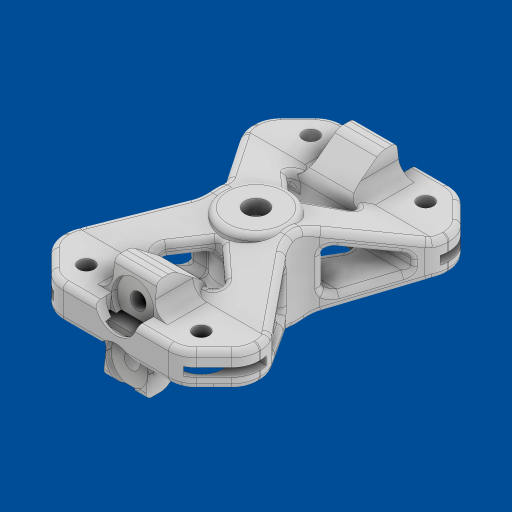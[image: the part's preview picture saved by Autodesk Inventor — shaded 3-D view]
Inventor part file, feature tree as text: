
AUTODESK INVENTOR PART (.ipt)
format: ipt  version: 2023 (Build 270158000, 158)  size: 1,712,640 bytes
history: native  units: mm
features: extrude x20, fillet x18, sketch x6, chamfer x4, mirror x3, plane x1, loft x1, other x1
ambient origin geometry x8: Origin, YZ Plane, XZ Plane, XY Plane, X Axis, Y Axis, Z Axis, Center Point
bodies: Body1 (feature_tree)
feature tree (54):
  sketch  "Sketch1"  dims[d13=261.822mm d14=7.45mm]
  plane  "Work Plane1"
  sketch  "Sketch2"  dims[d15=27.223mm d17=1.0mm]
  extrude  "Extrusion26"  Depth=7.45mm
  extrude  "Extrusion27"  Depth=1.0mm
  loft  "Loft4"
  extrude  "Extrusion30"  Depth=1.0mm
  extrude  "Extrusion32"  Depth=1.0mm
  extrude  "Extrusion33"  Depth=15.0mm
  chamfer  "Chamfer7"  Distance=65.0mm
  chamfer  "Chamfer8"  Distance=12.0mm
  fillet  "Fillet9"  Radius=1.0mm
  mirror  "Mirror1"
  extrude  "Extrusion45"  Depth=15.0mm
  extrude  "Extrusion48"  Depth=15.0mm TaperAngle=0.0deg
  extrude  "Extrusion49"  Depth=15.0mm
  sketch  "Sketch17"  dims[d23=2.0mm d25=1.0mm]
  extrude  "Extrusion51"  Depth=15.0mm
  fillet  "Fillet30"  Radius=30.0mm
  extrude  "Extrusion54"  Depth=5.0mm TaperAngle=0.0deg
  extrude  "Extrusion55"  Depth=15.0mm
  extrude  "Extrusion57"  TaperAngle=0.0deg  [1 undecoded]
  extrude  "Extrusion58"  TaperAngle=0.0deg  [1 undecoded]
  extrude  "Extrusion59"  Depth=15.0mm TaperAngle=0.0deg
  extrude  "Extrusion60"  Depth=15.0mm
  chamfer  "Chamfer15"  Distance=15.0mm
  chamfer  "Chamfer16"  Distance=15.0mm
  mirror  "Mirror3"
  extrude  "Extrusion61"  Depth=15.0mm TaperAngle=45.0deg
  extrude  "Extrusion62"  Depth=15.0mm TaperAngle=45.0deg
  extrude  "Extrusion63"  Depth=10.0mm
  fillet  "Fillet34"  Radius=15.0mm
  fillet  "Fillet35"  Radius=30.0mm
  fillet  "Fillet37"  Radius=14.0mm
  fillet  "Fillet38"  Radius=100.0mm
  extrude  "Extrusion64"  Depth=10.0mm
  mirror  "Mirror4"
  fillet  "Fillet39"  Radius=100.0mm
  fillet  "Fillet42"  Radius=15.0mm
  fillet  "Fillet43"  Radius=15.0mm
  fillet  "Fillet44"  Radius=15.0mm
  fillet  "Fillet45"  Radius=15.0mm
  fillet  "Fillet46"  Radius=7.5mm
  fillet  "Fillet47"  Radius=15.0mm
  fillet  "Fillet48"  Radius=5.5mm
  fillet  "Fillet49"  Radius=15.0mm
  fillet  "Fillet50"  Radius=2.5mm
  fillet  "Fillet51"  Radius=15.0mm
  fillet  "Fillet52"  Radius=15.0mm
  extrude  "Extrusion66"  Depth=15.0mm
  sketch  "Sketch12"  dims[d21=35.0mm d22=100.0mm]
  other  "Edges5"
  sketch  "Sketch18"  dims[d26=90.0deg d27=1.0mm]
  sketch  "Sketch19"  dims[d28=90.0deg d29=5.5mm d30=15.0mm d31=65.0mm d56=12.0mm d74=1.0mm d75=8.0mm d148=244.423mm d149=41.005864mm d150=244.423mm d151=5.5mm d152=5.5mm d153=5.5mm d154=15.0mm d155=15.0mm d156=18.0mm d157=5.5mm d158=160.0mm d159=7.0mm d160=0.0mm d161=8.0mm d162=24.0mm d163=30.0mm d164=0.0mm d165=5.0mm d166=0.0mm d167=19.96mm d170=0.0mm d171=90.0deg d172=0.0mm d173=90.0deg d178=2.0mm d179=0.0mm d180=2.0mm d183=15.0mm d184=0.0mm d185=15.0mm d186=0.0mm d206=12.0mm d207=12.0mm d208=45.0deg d209=12.0mm d210=12.0mm d211=45.0deg d212=10.0mm d256=15.0mm d257=30.0mm d258=0.0mm d271=14.0mm d272=100.0mm d273=10.0mm d274=100.0mm d276=15.0mm d277=0.0mm d287=15.0mm d288=0.0mm d289=15.0mm d290=15.0mm d291=7.5mm d292=15.0mm d293=5.5mm d296=15.0mm d297=2.5mm d298=15.0mm d299=15.0mm d300=7.5mm d301=15.0mm d302=5.5mm d303=15.0mm d304=0.0mm d310=2.0mm d311=2.0mm d312=0.0mm d313=5.0mm d316=5.0mm d317=5.0mm d318=16.0mm d319=100.0mm d320=0.0mm d324=35.0mm d325=0.0mm d326=40.0mm d327=0.0mm d328=20.0mm d329=0.0mm d330=12.0mm d331=0.0mm d333=5.0mm d334=12.0mm d335=9.168mm d336=45.0deg d337=15.0mm d338=10.835mm d339=45.0deg d341=5.0mm d342=30.0mm d343=0.0mm d344=30.0mm d345=0.0mm d346=30.0mm d347=0.0mm d348=10.0mm d349=10.0mm d351=2.0mm d352=2.0mm d353=2.0mm d354=0.0mm d355=2.0mm d358=2.0mm d359=2.0mm d360=2.0mm d361=2.0mm d362=2.0mm d363=2.0mm d364=2.0mm d365=2.0mm d366=2.0mm d367=5.0mm d368=5.0mm d369=1.0mm d370=0.0mm d373=10.0mm d374=0.0mm d375=15.0mm d376=0.0mm d76=0.5mm d77=0.872665mm d144=0.5mm d145=0.872665mm d146=0.5mm d147=0.872665mm d241=0.0mm d242=0.0mm d243=0.0mm d244=0.0mm d268=0.0mm d269=0.0mm d270=0.0mm d350=0.0mm d357=0.0mm]
note: 2 required parameter values undecoded (feature->parameter linkage not recoverable at this tier; creation-order binding heuristic only, values carry confidence <= 0.55)
